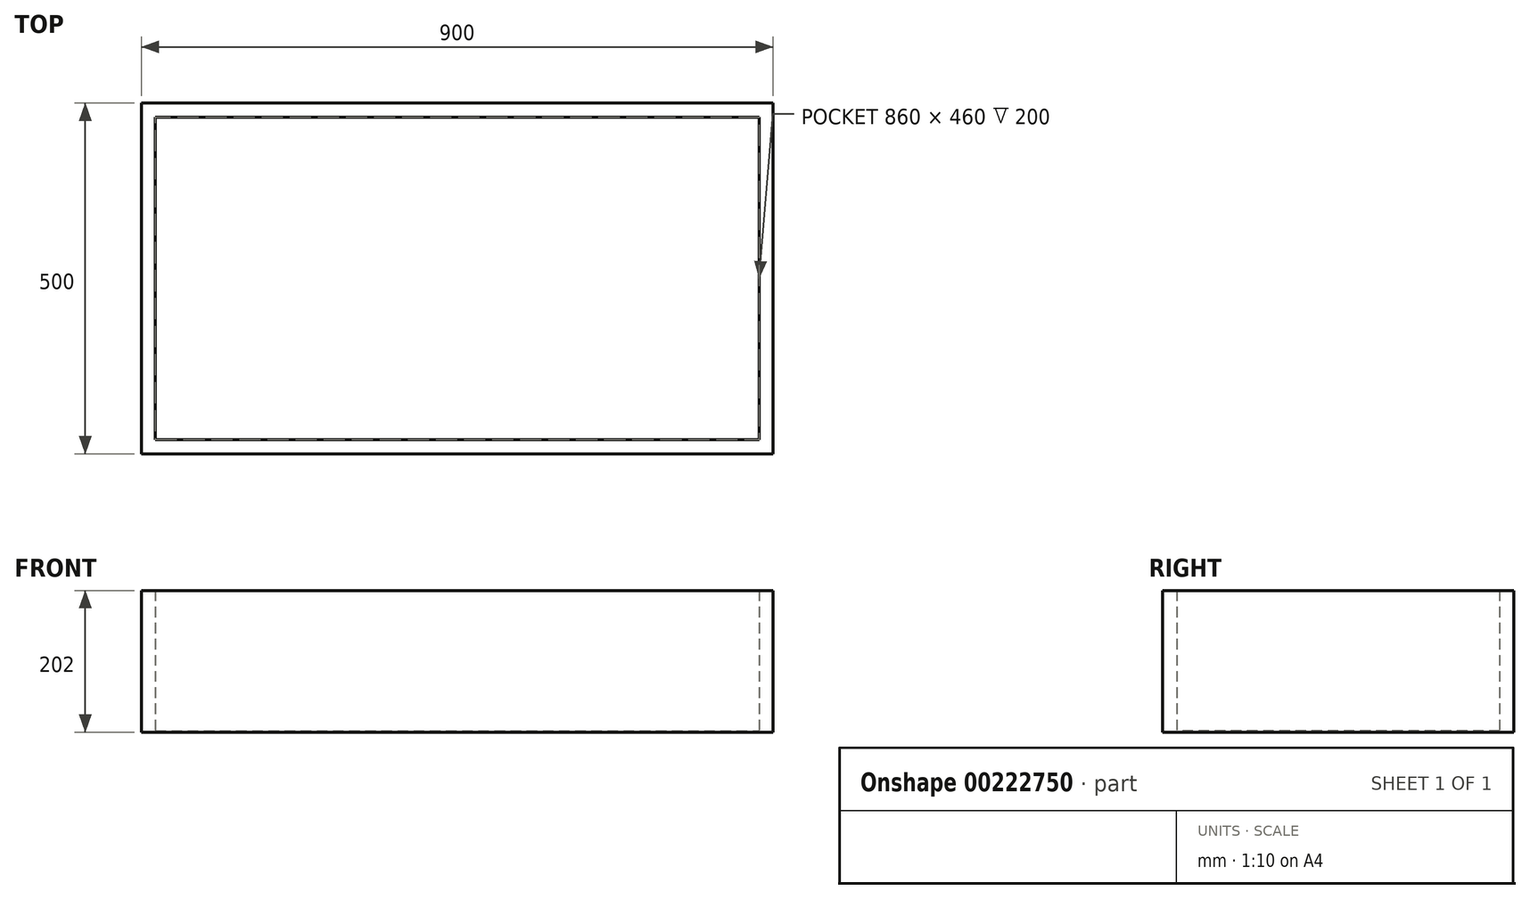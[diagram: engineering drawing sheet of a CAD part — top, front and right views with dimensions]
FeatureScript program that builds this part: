
annotation { "Feature Type Name" : "Feature", "Feature Type Description" : "" }
export const myFeature = defineFeature(function(context is Context, id is Id, definition is map)
    precondition{}
    {
        {
            var Q0;
            Q0=qCreatedBy(makeId("Top.planeOp"),FACE);
            var sketch = newSketch(context, id + "F0", { "sketchPlane" : qUnion([Q0])});
            skLineSegment(sketch, "E0.bottom", {"start": v(-388.35, 288.4) * mm, "end": v(511.65, 288.4) * mm});
            skLineSegment(sketch, "E0.top", {"start": v(-388.35, -211.6) * mm, "end": v(511.65, -211.6) * mm});
            skLineSegment(sketch, "E0.left", {"start": v(-388.35, 288.4) * mm, "end": v(-388.35, -211.6) * mm});
            skLineSegment(sketch, "E0.right", {"start": v(511.65, 288.4) * mm, "end": v(511.65, -211.6) * mm});
            skLineSegment(sketch, "E1.0", {"start": v(-368.35, 268.4) * mm, "end": v(491.65, 268.4) * mm});
            skLineSegment(sketch, "E1.1", {"start": v(-368.35, 268.4) * mm, "end": v(-368.35, -191.6) * mm});
            skLineSegment(sketch, "E1.2", {"start": v(-368.35, -191.6) * mm, "end": v(491.65, -191.6) * mm});
            skLineSegment(sketch, "E1.3", {"start": v(491.65, 268.4) * mm, "end": v(491.65, -191.6) * mm});
            skSolve(sketch);
        }
        {
            var Q0;
            Q0=makeQuery(id+"F0.imprint","IMPRINT",FACE,{"disambiguationData":[TD([[makeQuery(id+"F0.imprint","IMPRINT",EDGE,{"derivedFrom":sQuery(id+"F0.wireOp",EDGE,"E1.0")}),-1.0]])]});
            var Q1;
            Q1=makeQuery(id+"F0.imprint","IMPRINT",FACE,{"disambiguationData":[TD([[makeQuery(id+"F0.imprint","IMPRINT",EDGE,{"derivedFrom":sQuery(id+"F0.wireOp",EDGE,"E0.bottom")}),-1.0]])]});
            extrude(context, id + "F1", {"entities" : qUnion([Q0, Q1]), "oppositeDirection" : true, "depth" : 2 * mm});
        }
        {
            var Q0;
            Q0=makeQuery(id+"F0.imprint","IMPRINT",FACE,{"disambiguationData":[TD([[makeQuery(id+"F0.imprint","IMPRINT",EDGE,{"derivedFrom":sQuery(id+"F0.wireOp",EDGE,"E0.bottom")}),-1.0]])]});
            extrude(context, id + "F2", {"entities" : qUnion([Q0]), "operationType" : NewBodyOperationType.ADD, "depth" : 200 * mm});
        }
    });
